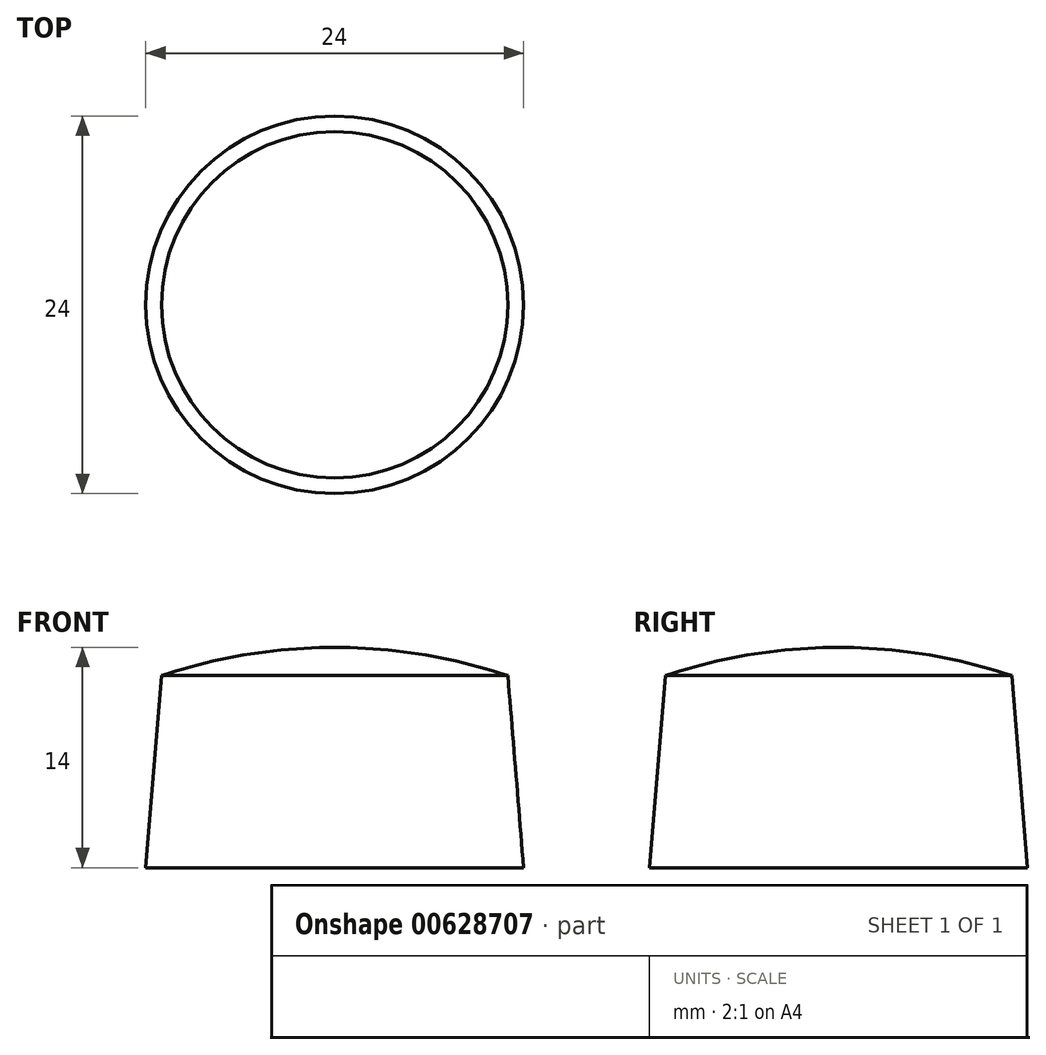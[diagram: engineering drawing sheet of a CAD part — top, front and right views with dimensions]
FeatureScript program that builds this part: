
annotation { "Feature Type Name" : "Feature", "Feature Type Description" : "" }
export const myFeature = defineFeature(function(context is Context, id is Id, definition is map)
    precondition{}
    {
        {
            var Q0;
            Q0=qCreatedBy(makeId("Front.planeOp"),FACE);
            var sketch = newSketch(context, id + "F0", { "sketchPlane" : qUnion([Q0])});
            skLineSegment(sketch, "E0", {"start": v(0, 58.84) * mm, "end": v(0, -62.47) * mm, "construction": true});
            skLineSegment(sketch, "E1", {"start": v(0, -7) * mm, "end": v(-12, -7) * mm});
            skLineSegment(sketch, "E2", {"start": v(-12, -7) * mm, "end": v(-11, 5.2) * mm});
            skArc(sketch, "E3", {"start": v(0, 7) * mm, "mid": v(-5.57, 6.53) * mm, "end": v(-11, 5.2) * mm});
            skLineSegment(sketch, "E4", {"start": v(0, 7) * mm, "end": v(0, -7) * mm});
            skSolve(sketch);
        }
        {
            var Q0;
            Q0 = qSketchRegion(id + "F0", true);
            var Q1;
            Q1=sQuery(id+"F0.wireOp",EDGE,"E0");
            revolve(context, id + "F1", {"entities" : qUnion([Q0]), "axis" : qUnion([Q1]), "revolveType" : RevolveType.FULL});
        }
    });
